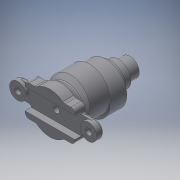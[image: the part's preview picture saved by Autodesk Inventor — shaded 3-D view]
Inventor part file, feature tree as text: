
AUTODESK INVENTOR PART (.ipt)
format: ipt  version: 2019.4 (Build 234330000, 330)  size: 359,936 bytes
history: native  units: mm
features: sketch x15, extrude x13, fillet x4, projected_geometry x4, revolve x1, chamfer x1, hole x1
ambient origin geometry x8: Origin, YZ Plane, XZ Plane, XY Plane, X Axis, Y Axis, Z Axis, Center Point
bodies: Solid1 (feature_tree)
feature tree (39):
  extrude  "Extrusion1"  Depth=1.0mm
  revolve  "Revolution1"  [1 undecoded]
  extrude  "Extrusion2"  Depth=4.0mm
  chamfer  "Chamfer1"  Distance=8.0mm
  extrude  "Extrusion6"  Depth=2.0mm TaperAngle=45.0deg
  extrude  "Extrusion7"  Depth=2.0mm TaperAngle=0.0deg
  extrude  "Extrusion8"  Depth=4.0mm TaperAngle=0.0deg
  extrude  "Extrusion9"  Depth=8.0mm
  hole  "Hole1"  [1 undecoded]
  extrude  "Extrusion10"  Depth=1.5mm TaperAngle=0.0deg
  extrude  "Extrusion11"  TaperAngle=0.0deg  [1 undecoded]
  fillet  "Fillet7"  Radius=20.0mm
  extrude  "Extrusion13"  Depth=24.0mm
  extrude  "Extrusion14"  Depth=1.0mm TaperAngle=0.0deg
  fillet  "Fillet9"  Radius=2.0mm
  extrude  "Extrusion15"  Depth=1.0mm TaperAngle=0.0deg
  extrude  "Extrusion16"  Depth=1.0mm
  extrude  "Extrusion17"  Depth=1.0mm TaperAngle=0.0deg
  fillet  "Fillet10"  Radius=2.0mm
  fillet  "Fillet11"  Radius=9.0mm
  sketch  "Sketch1"  dims[d0=3.0mm d1=1.0mm]
  sketch  "Sketch2"  dims[d2=19.95mm d3=14.0mm d4=0.0mm]
  sketch  "Sketch3"  dims[d5=3.0mm d6=4.0mm]
  projected_geometry  "Projected Loop1"
  sketch  "Sketch7"  dims[d7=4.0mm]
  sketch  "Sketch8"  dims[d8=90.0deg]
  sketch  "Sketch9"  dims[d10=19.95mm d11=8.0mm d12=0.0mm]
  sketch  "Sketch10"  dims[d13=1.0mm d18=0.5mm d19=2.0mm d20=45.0deg]
  projected_geometry  "Projected Loop2"
  sketch  "Sketch11"  dims[d33=15.0mm d34=2.0mm d35=0.0mm]
  sketch  "Sketch12"  dims[d36=11.95mm d37=4.0mm d38=0.0mm]
  sketch  "Sketch13"  dims[d39=34.0mm d40=8.0mm]
  sketch  "Sketch16"  dims[d41=2.0mm d42=0.0mm d43=8.0mm]
  projected_geometry  "Projected Loop3"
  sketch  "Sketch17"  dims[d44=8.0mm d45=1.5mm d46=0.0mm]
  sketch  "Sketch18"  dims[d47=3.1mm d48=5.2mm d49=6.5mm d50=2.0mm d51=90.0deg d52=10.0mm d53=0.0mm d58=0.0mm d59=20.0mm]
  sketch  "Sketch19"  dims[d60=3.0mm d61=0.0mm d63=24.0mm]
  projected_geometry  "Projected Loop4"
  sketch  "Sketch20"  dims[d64=15.0mm d65=3.0mm d66=0.0mm d68=2.0mm d74=3.0mm d75=0.0mm d76=10.1mm d77=3.0mm d78=0.0mm d79=2.0mm d80=9.0mm d81=5.5mm d82=0.0mm d83=6.0mm d84=3.0mm d85=0.0mm d86=2.5mm d87=0.0mm d88=1.0mm d89=1.0mm]
note: 3 required parameter values undecoded (feature->parameter linkage not recoverable at this tier; creation-order binding heuristic only, values carry confidence <= 0.55)